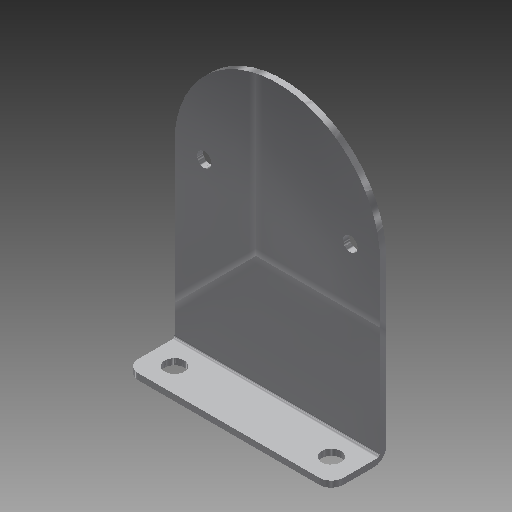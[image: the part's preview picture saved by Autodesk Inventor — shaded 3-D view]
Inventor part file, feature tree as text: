
AUTODESK INVENTOR PART (.ipt)
format: ipt  version: 2017 (Build 210142000, 142)  size: 140,800 bytes
history: native  units: in
note: dims shown in document units (in); Inventor stores cm internally (conversion verified against a paired STEP export)
features: fillet x3, hole x3, sketch x3, extrude x2, reference x2
ambient origin geometry x8: Origin, YZ Plane, XZ Plane, XY Plane, X Axis, Y Axis, Z Axis, Center Point
bodies: Solid1 (feature_tree)
feature tree (13):
  extrude  "Extrusion1"  Depth=0.0625in
  extrude  "Extrusion2"  Depth=0.125in
  fillet  "Fillet1"  Radius=0.0312in
  hole  "Hole1"  [1 undecoded]
  fillet  "Fillet2"  Radius=0.75in
  hole  "Hole2"  [1 undecoded]
  hole  "Hole3"  [1 undecoded]
  fillet  "Fillet3"  [1 undecoded]
  sketch  "Sketch1"  dims[d0=0.0625in d1=0.0in d2=0.0625in]
  reference  "Reference1"
  sketch  "Sketch2"  dims[d3=0.5in d4=0.0in d5=0.125in]
  sketch  "Sketch3"  dims[d6=0.25in d16=0.25in d8=0.201in d9=0.75in d10=0.385in d11=0.25in d12=0.5635in d13=1.0in d14=0.8108in d15=0.0312in d17=0.25in d18=0.25in d19=0.201in d20=0.75in d21=0.385in d22=0.25in d23=0.5635in d24=1.0in d25=0.8108in d26=0.75in d27=0.75in d28=0.15in d29=0.75in d30=0.385in d31=0.25in d32=0.5635in d33=1.0in d34=0.8108in d35=0.125in]
  reference  "Reference3"
note: 4 required parameter values undecoded (feature->parameter linkage not recoverable at this tier; creation-order binding heuristic only, values carry confidence <= 0.55)
